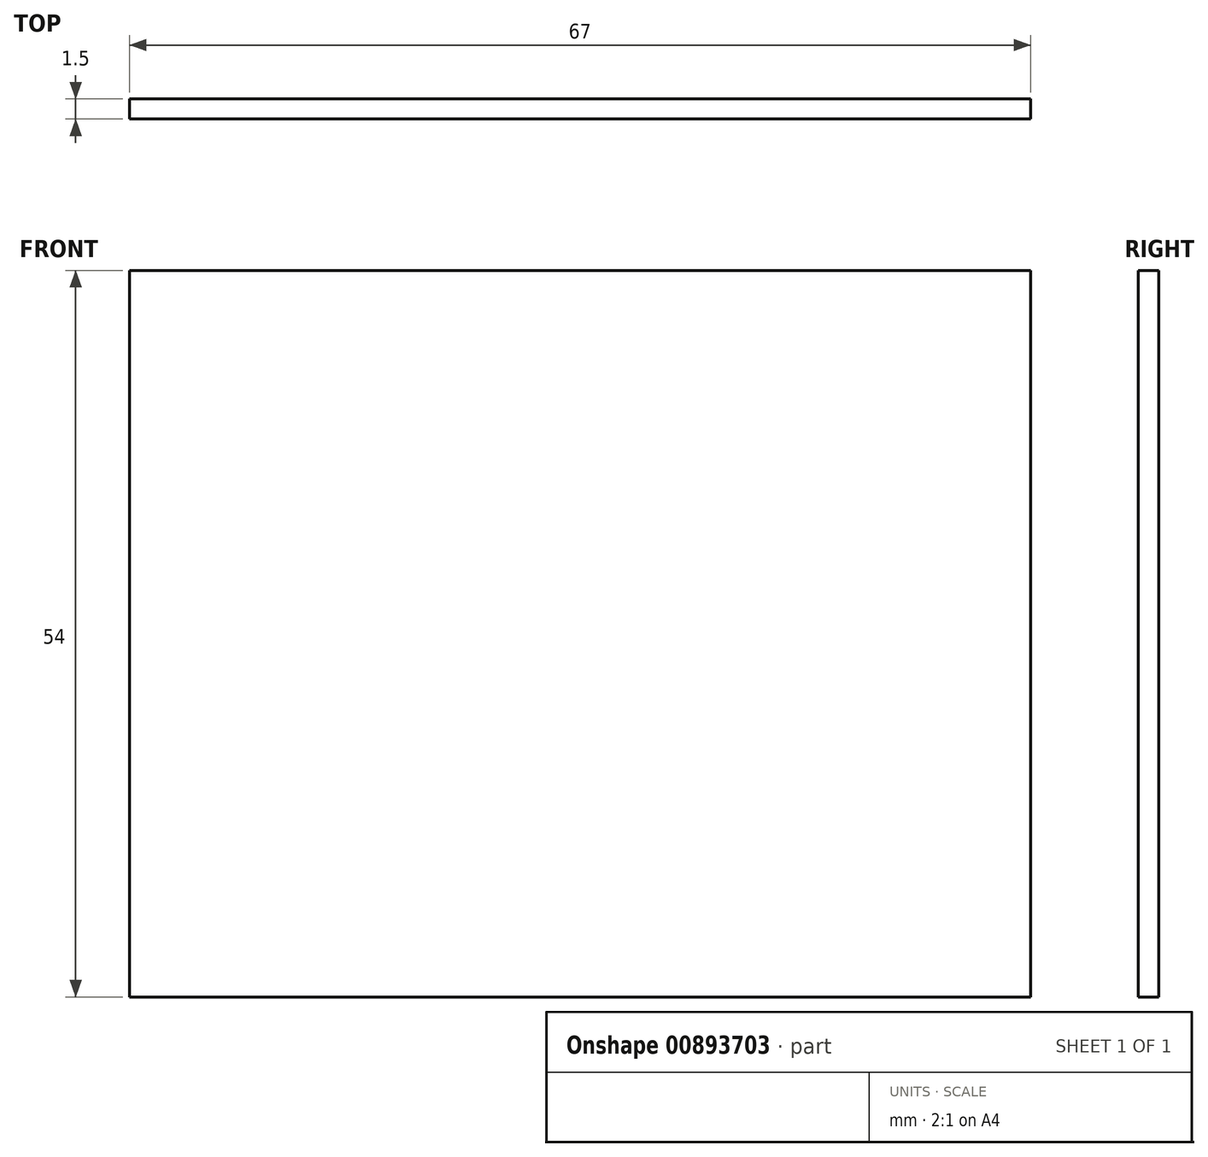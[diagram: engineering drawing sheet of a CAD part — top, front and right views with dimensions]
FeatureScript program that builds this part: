
annotation { "Feature Type Name" : "Feature", "Feature Type Description" : "" }
export const myFeature = defineFeature(function(context is Context, id is Id, definition is map)
    precondition{}
    {
        {
            var Q0;
            Q0=qCreatedBy(makeId("Front.planeOp"),FACE);
            var sketch = newSketch(context, id + "F0", { "sketchPlane" : qUnion([Q0])});
            skLineSegment(sketch, "E0.bottom", {"start": v(33.5, 27) * mm, "end": v(-33.5, 27) * mm});
            skLineSegment(sketch, "E0.top", {"start": v(33.5, -27) * mm, "end": v(-33.5, -27) * mm});
            skLineSegment(sketch, "E0.left", {"start": v(33.5, 27) * mm, "end": v(33.5, -27) * mm});
            skLineSegment(sketch, "E0.right", {"start": v(-33.5, 27) * mm, "end": v(-33.5, -27) * mm});
            skPoint(sketch, "E0.middle", {"position": v(0, 0) * mm});
            skSolve(sketch);
        }
        {
            var Q0;
            Q0=makeQuery(id+"F0.imprint","IMPRINT",FACE,{"disambiguationData":[TD([[makeQuery(id+"F0.imprint","IMPRINT",EDGE,{"derivedFrom":sQuery(id+"F0.wireOp",EDGE,"E0.bottom")}),1.0]])]});
            extrude(context, id + "F1", {"entities" : qUnion([Q0]), "oppositeDirection" : true, "depth" : 1.5 * mm, "offsetDistance" : 25 * mm});
        }
    });
